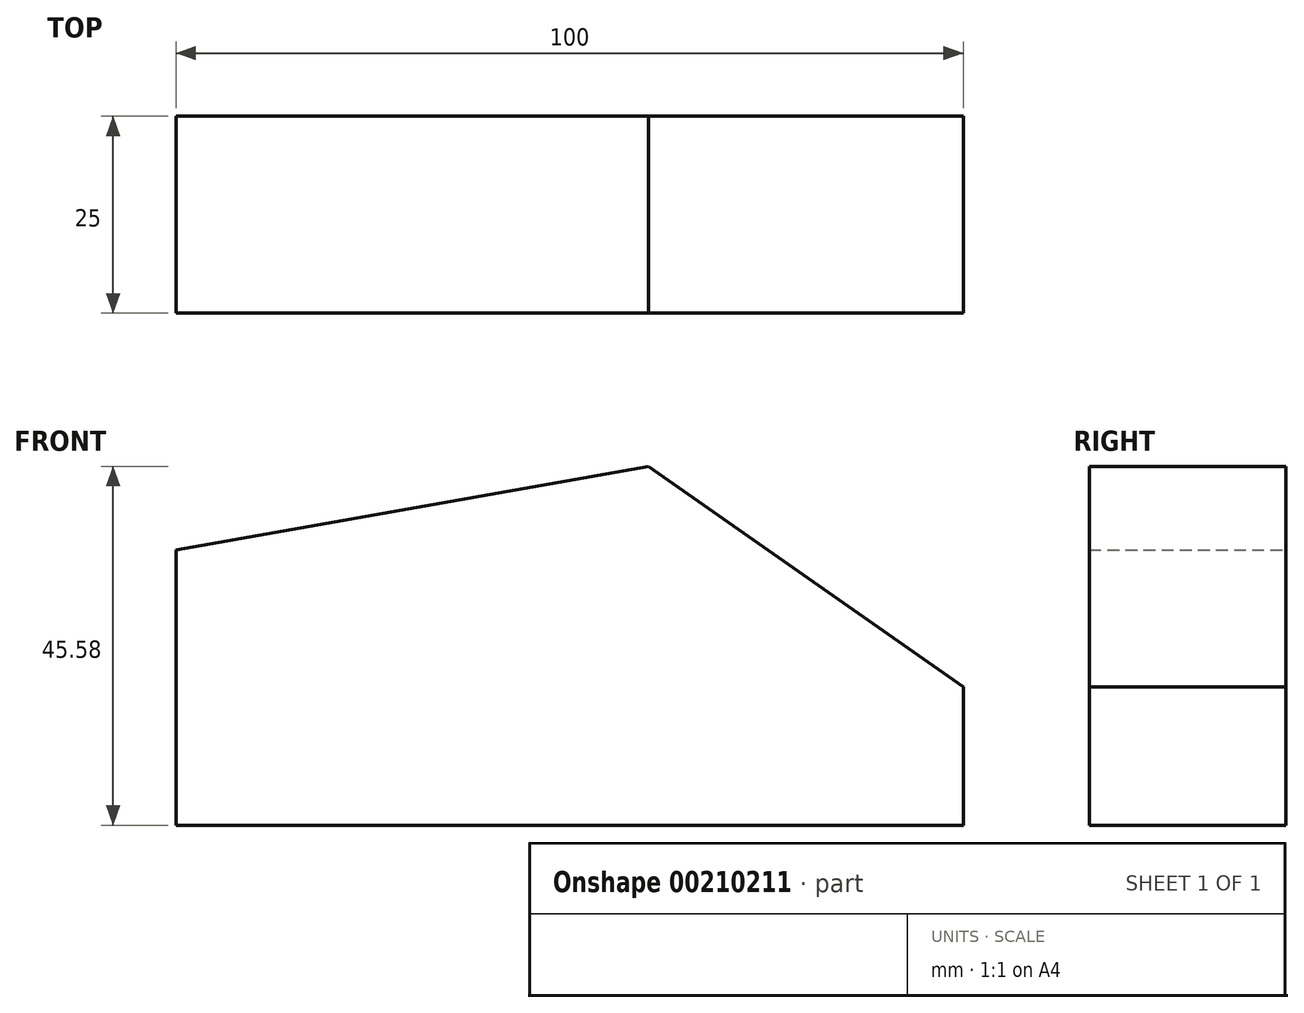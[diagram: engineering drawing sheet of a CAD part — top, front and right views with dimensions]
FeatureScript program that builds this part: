
annotation { "Feature Type Name" : "Feature", "Feature Type Description" : "" }
export const myFeature = defineFeature(function(context is Context, id is Id, definition is map)
    precondition{}
    {
        {
            var Q0;
            Q0=qCreatedBy(makeId("Front.planeOp"),FACE);
            var sketch = newSketch(context, id + "F0", { "sketchPlane" : qUnion([Q0])});
            skLineSegment(sketch, "E0", {"start": v(0, 0) * mm, "end": v(100, 0) * mm});
            skLineSegment(sketch, "E1", {"start": v(100, 0) * mm, "end": v(100, 17.57) * mm});
            skLineSegment(sketch, "E2", {"start": v(100, 17.57) * mm, "end": v(60, 45.58) * mm});
            skLineSegment(sketch, "E3", {"start": v(60, 45.58) * mm, "end": v(0, 35) * mm});
            skLineSegment(sketch, "E4", {"start": v(0, 35) * mm, "end": v(0, 0) * mm});
            skSolve(sketch);
        }
        {
            var Q0;
            Q0 = qSketchRegion(id + "F0", true);
            extrude(context, id + "F1", {"entities" : qUnion([Q0]), "depth" : 25 * mm});
        }
    });
